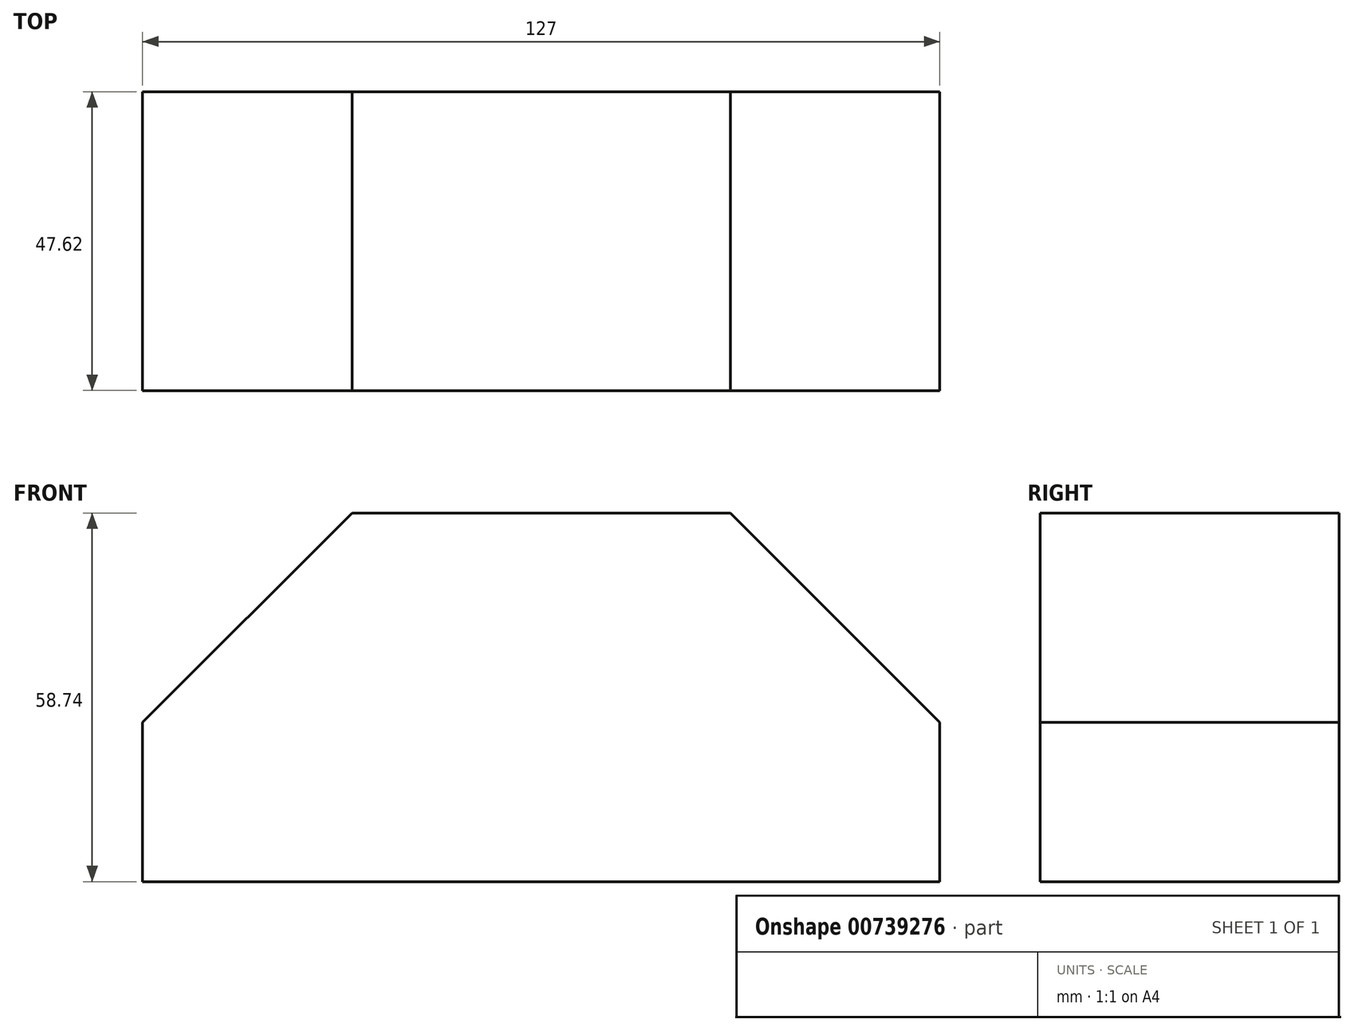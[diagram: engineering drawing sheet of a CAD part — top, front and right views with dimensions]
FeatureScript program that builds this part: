
annotation { "Feature Type Name" : "Feature", "Feature Type Description" : "" }
export const myFeature = defineFeature(function(context is Context, id is Id, definition is map)
    precondition{}
    {
        {
            var Q0;
            Q0=qCreatedBy(makeId("Front.planeOp"),FACE);
            var sketch = newSketch(context, id + "F0", { "sketchPlane" : qUnion([Q0])});
            skLineSegment(sketch, "E0", {"start": v(0, 0) * mm, "end": v(-127, 0) * mm});
            skLineSegment(sketch, "E1", {"start": v(-127, 0) * mm, "end": v(-127, 25.39) * mm});
            skLineSegment(sketch, "E2", {"start": v(-127, 25.39) * mm, "end": v(-93.65, 58.74) * mm});
            skLineSegment(sketch, "E3", {"start": v(-93.65, 58.74) * mm, "end": v(-33.35, 58.74) * mm});
            skLineSegment(sketch, "E4", {"start": v(-33.35, 58.74) * mm, "end": v(0, 25.39) * mm});
            skLineSegment(sketch, "E5", {"start": v(0, 25.39) * mm, "end": v(0, 0) * mm});
            skSolve(sketch);
        }
        {
            var Q0;
            Q0=makeQuery(id+"F0.imprint","IMPRINT",FACE,{"disambiguationData":[TD([[makeQuery(id+"F0.imprint","IMPRINT",EDGE,{"derivedFrom":sQuery(id+"F0.wireOp",EDGE,"E0")}),-1.0]])]});
            extrude(context, id + "F1", {"entities" : qUnion([Q0]), "depth" : 47.62 * mm, "offsetDistance" : 25.4 * mm});
        }
    });
